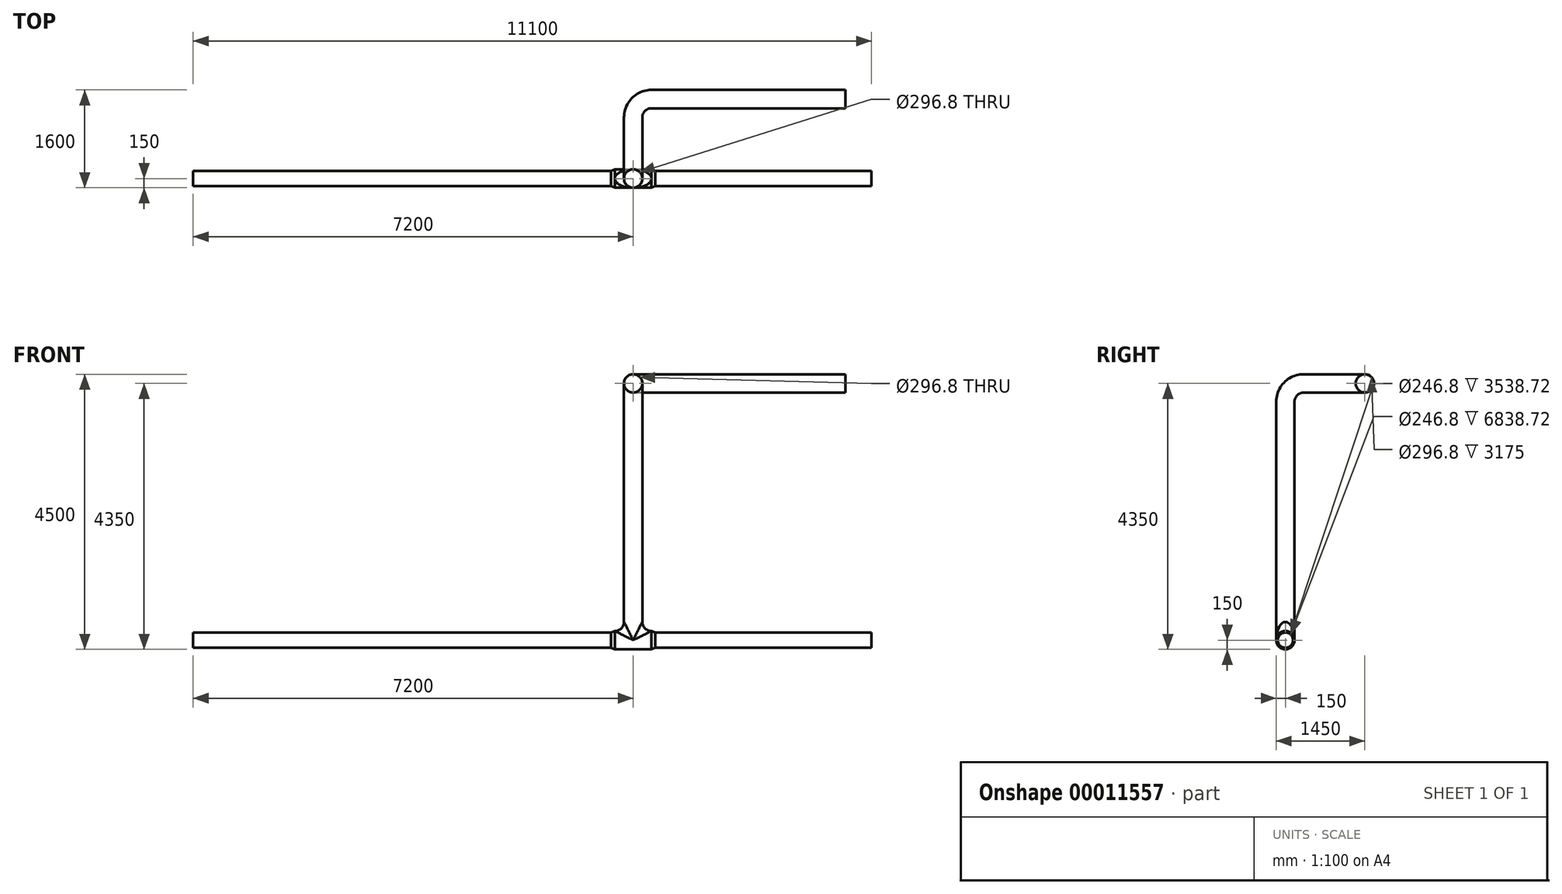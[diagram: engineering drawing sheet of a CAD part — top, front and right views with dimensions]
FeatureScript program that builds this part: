
annotation { "Feature Type Name" : "Feature", "Feature Type Description" : "" }
export const myFeature = defineFeature(function(context is Context, id is Id, definition is map)
    precondition{}
    {
        {
            var Q0;
            Q0=qCreatedBy(makeId("Right.planeOp"),FACE);
            var sketch = newSketch(context, id + "F0", { "sketchPlane" : qUnion([Q0])});
            skCircle(sketch, "E0", {"center": v(0, 0) * mm, "radius": 125 * mm});
            skSolve(sketch);
        }
        {
            var Q0;
            Q0=makeQuery(id+"F0.imprint","IMPRINT",FACE,{"disambiguationData":[TD([[makeQuery(id+"F0.imprint","IMPRINT",EDGE,{"derivedFrom":sQuery(id+"F0.wireOp",EDGE,"E0")}),1.0]])]});
            extrude(context, id + "F1", {"entities" : qUnion([Q0]), "depth" : 3900 * mm, "hasSecondDirection" : true, "secondDirectionOppositeDirection" : true, "secondDirectionDepth" : 7200 * mm});
        }
        {
            var Q0;
            Q0=qCreatedBy(makeId("Right.planeOp"),FACE);
            var sketch = newSketch(context, id + "F2", { "sketchPlane" : qUnion([Q0])});
            skCircle(sketch, "E1", {"center": v(0, 0) * mm, "radius": 150 * mm});
            skSolve(sketch);
        }
        {
            var Q0;
            Q0 = qSketchRegion(id + "F2", true);
            extrude(context, id + "F3", {"entities" : qUnion([Q0]), "operationType" : NewBodyOperationType.ADD, "endBound" : BoundingType.SYMMETRIC, "depth" : 600 * mm});
        }
        {
            var Q0;
            Q0=makeQuery(id+"F3.boolean.opBoolean","INTERSECT",EDGE,{"derivedFrom":[makeQuery(id+"F1.opExtrude","SWEPT_FACE",FACE,{"disambiguationData":[OSD([sQuery(id+"F0.wireOp",EDGE,"E0")])]}),makeQuery(id+"F3.opExtrude","CAP_FACE",FACE,{"disambiguationData":[OSD([sQuery(id+"F2.wireOp",EDGE,"E1")])],"isStart":false})]});
            chamfer(context, id + "F4", {"entities" : qUnion([Q0]), "chamferType" : ChamferType.TWO_OFFSETS, "width1" : 60 * mm, "oppositeDirection" : false, "width2" : 25 * mm, "tangentPropagation" : true});
        }
        {
            var Q0;
            Q0=makeQuery(id+"F3.boolean.opBoolean","INTERSECT",EDGE,{"derivedFrom":[makeQuery(id+"F1.opExtrude","SWEPT_FACE",FACE,{"disambiguationData":[OSD([sQuery(id+"F0.wireOp",EDGE,"E0")])]}),makeQuery(id+"F3.opExtrude","CAP_FACE",FACE,{"disambiguationData":[OSD([sQuery(id+"F2.wireOp",EDGE,"E1")])],"isStart":true})]});
            chamfer(context, id + "F5", {"entities" : qUnion([Q0]), "chamferType" : ChamferType.TWO_OFFSETS, "width1" : 60 * mm, "oppositeDirection" : true, "width2" : 25 * mm, "tangentPropagation" : true});
        }
        {
            var Q0;
            Q0=qCreatedBy(makeId("Top.planeOp"),FACE);
            var sketch = newSketch(context, id + "F6", { "sketchPlane" : qUnion([Q0])});
            skCircle(sketch, "E2", {"center": v(0, 0) * mm, "radius": 150 * mm});
            skSolve(sketch);
        }
        {
            var Q0;
            Q0 = qSketchRegion(id + "F6", true);
            extrude(context, id + "F7", {"entities" : qUnion([Q0]), "operationType" : NewBodyOperationType.ADD, "depth" : 300 * mm});
        }
        {
            var Q0;
            Q0=makeQuery(id+"F7.boolean.opBoolean","INTERSECT",EDGE,{"disambiguationData":[OD(0.0)],"derivedFrom":[makeQuery(id+"F3.opExtrude","SWEPT_FACE",FACE,{"disambiguationData":[OSD([sQuery(id+"F2.wireOp",EDGE,"E1")])]}),makeQuery(id+"F7.opExtrude","SWEPT_FACE",FACE,{"disambiguationData":[OSD([sQuery(id+"F6.wireOp",EDGE,"E2")])]})]});
            var Q1;
            Q1=makeQuery(id+"F7.boolean.opBoolean","INTERSECT",EDGE,{"disambiguationData":[OD(1.0)],"derivedFrom":[makeQuery(id+"F3.opExtrude","SWEPT_FACE",FACE,{"disambiguationData":[OSD([sQuery(id+"F2.wireOp",EDGE,"E1")])]}),makeQuery(id+"F7.opExtrude","SWEPT_FACE",FACE,{"disambiguationData":[OSD([sQuery(id+"F6.wireOp",EDGE,"E2")])]})]});
            fillet(context, id + "F8", {"entities" : qUnion([Q0, Q1]), "radius" : 150 * mm, "tangentPropagation" : true, "allowEdgeOverflow" : false});
        }
        {
            var Q0;
            Q0=qCreatedBy(makeId("Right.planeOp"),FACE);
            var sketch = newSketch(context, id + "F9", { "sketchPlane" : qUnion([Q0])});
            skLineSegment(sketch, "E3", {"start": v(0, 300) * mm, "end": v(0, 3900) * mm});
            skLineSegment(sketch, "E4", {"start": v(300, 4200) * mm, "end": v(1000, 4200) * mm});
            skArc(sketch, "E5.filletArc", {"start": v(300, 4200) * mm, "mid": v(87.87, 4112.13) * mm, "end": v(0, 3900) * mm});
            skSolve(sketch);
        }
        {
            var Q0;
            Q0=qCreatedBy(makeId("Top.planeOp"),FACE);
            cPlane(context, id + "F10", {"entities" : qUnion([Q0]), "cplaneType" : CPlaneType.OFFSET, "offset" : 4200 * mm, "width" : 150 * mm, "height" : 150 * mm});
        }
        {
            var Q0;
            Q0=qCreatedBy(id+"F10.planeOp",FACE);
            var sketch = newSketch(context, id + "F11", { "sketchPlane" : qUnion([Q0])});
            skLineSegment(sketch, "E6", {"start": v(0, 1000) * mm, "end": v(0, 1000) * mm});
            skLineSegment(sketch, "E7", {"start": v(300, 1300) * mm, "end": v(3475, 1300) * mm});
            skArc(sketch, "E8.filletArc", {"start": v(300, 1300) * mm, "mid": v(87.87, 1212.13) * mm, "end": v(0, 1000) * mm});
            skSolve(sketch);
        }
        {
            var Q0;
            Q0=makeQuery(id+"F7.opExtrude","CAP_FACE",FACE,{"disambiguationData":[OSD([sQuery(id+"F6.wireOp",EDGE,"E2")])],"isStart":false});
            var sketch = newSketch(context, id + "F12", { "sketchPlane" : qUnion([Q0])});
            skCircle(sketch, "E9", {"center": v(0, 0) * mm, "radius": 150 * mm});
            skSolve(sketch);
        }
        {
            var Q0;
            Q0 = qSketchRegion(id + "F12", true);
            var Q1;
            Q1 = qBodyType(qCreatedBy(id + "F9" ,EDGE), BodyType.WIRE);
            var Q2;
            Q2 = qBodyType(qCreatedBy(id + "F11" ,EDGE), BodyType.WIRE);
            sweep(context, id + "F13", {"operationType" : NewBodyOperationType.ADD, "profiles" : qUnion([Q0]), "path" : qUnion([Q1, Q2])});
        }
        {
            var Q0;
            Q0=makeQuery(id+"F13.opSweep","CAP_FACE",FACE,{"disambiguationData":[OSD([sQuery(id+"F11.wireOp",VERTEX,"E7.end"),sQuery(id+"F12.wireOp",EDGE,"E9")])],"isStart":false});
            shell(context, id + "F14", {"entities" : qUnion([Q0]), "thickness" : 1.6 * mm});
        }
    });
